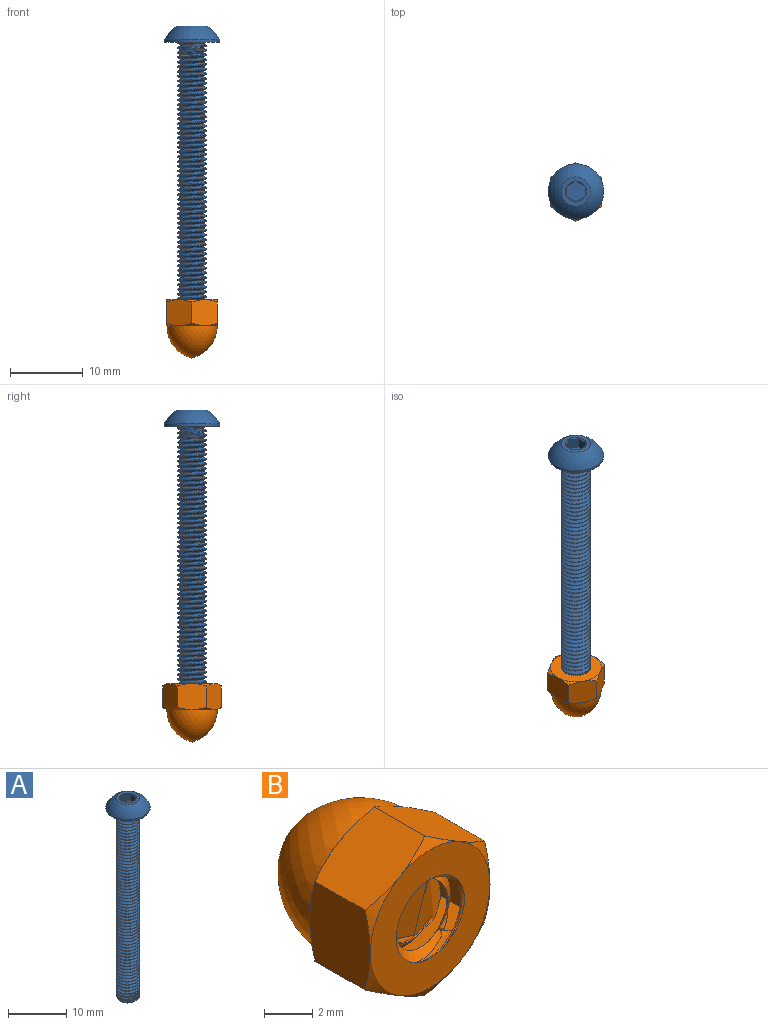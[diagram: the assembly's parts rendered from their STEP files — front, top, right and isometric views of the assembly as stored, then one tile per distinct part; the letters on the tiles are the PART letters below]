
ASSEMBLY  parts=2 mates=1
PART A: 24 faces, bbox 8.2x8.2x43.4 mm
  f0: cone r=1.44mm half-angle=45deg, axis (0,0,1), area 0.2mm2, adj f10,f18
  f1: cylinder r=3.8mm len=7.6mm, axis (0,0,1), area 7.9mm2, adj f2,f11
  f2: sphere r=4.23mm, area 49.8mm2, adj f1,f10
  f3: cone r=1.51mm half-angle=45deg, axis (0,0,1), area 4.2mm2, adj f4,f5,f6,f7,f8
  f4: cylinder r=2mm len=39.51mm, axis (0,0,-1), area 62.1mm2, adj f3,f6,f8,f9,f11
  f5: plane 3.03x3.03mm, normal (0,0,-1), area 7.2mm2, adj f3
  f6: bspline ~40.22x4.63mm, area 339.1mm2, adj f3,f4,f7,f11
  f7: cylinder r=1.58mm len=39.93mm, axis (0,0,-1), area 50.7mm2, adj f3,f6,f8,f11
  f8: bspline ~40.34x4.01mm, area 338.8mm2, adj f3,f4,f7,f9,f11
  f9: plane 0.14x0.08mm, normal (-0.24,0.97,0), area 0mm2, adj f4,f8,f11
  f10: plane 4.47x4.47mm, normal (0,0,1), area 6mm2, adj f0,f2,f12,f13,f14,f15,f16
  f11: plane 7.72x7.72mm, normal (0,0,-1), area 35.1mm2, adj f1,f4,f6,f7,f8,f9
  f12: cone r=1.44mm half-angle=45deg, axis (0,0,1), area 0mm2, adj f10,f19
  f13: cone r=1.44mm half-angle=45deg, axis (0,0,1), area 0mm2, adj f10,f20
  f14: cone r=1.44mm half-angle=45deg, axis (0,0,1), area 0mm2, adj f10,f21
  f15: cone r=1.44mm half-angle=45deg, axis (0,0,1), area 0mm2, adj f10,f22
  f16: cone r=1.44mm half-angle=45deg, axis (0,0,1), area 0mm2, adj f10,f23
  f17: plane 2.89x2.5mm, normal (0,0,1), area 5.4mm2, adj f18,f19,f20,f21,f22,f23
  f18: plane 1.68x1.58mm, normal (-1,0,0), area 2mm2, adj f0,f17,f19,f23
  f19: plane 2.09x1.8mm, normal (-0.5,-0.87,0), area 2mm2, adj f12,f17,f18,f20
  f20: plane 2.09x1.8mm, normal (0.5,-0.87,0), area 2mm2, adj f13,f17,f19,f21
  f21: plane 2.09x1.99mm, normal (1,0,0), area 2mm2, adj f14,f17,f20,f22
  f22: plane 2.09x1.8mm, normal (0.5,0.87,0), area 2mm2, adj f15,f17,f21,f23
  f23: plane 2.09x1.8mm, normal (-0.5,0.87,0), area 2mm2, adj f16,f17,f18,f22
PART B: 34 faces, bbox 8.4x8.6x8.4 mm
  f0: plane 7x7mm, normal (0,1,0), area 0.8mm2, adj f14,f15,f16,f17,f18,f19,f20
  f1: plane 3.89x3.83mm, normal (0.5,0,0.87), area 13.5mm2, adj f2,f6,f10,f11,f17,f18
  f2: plane 4.38x3.89mm, normal (1,0,0), area 13.5mm2, adj f1,f3,f9,f10,f16,f17
  f3: plane 3.89x3.83mm, normal (0.5,0,-0.87), area 13.5mm2, adj f2,f4,f8,f9,f15,f16
  f4: plane 3.89x3.83mm, normal (-0.5,0,-0.87), area 13.5mm2, adj f3,f5,f7,f8,f14,f15
  f5: plane 4.38x3.89mm, normal (-1,0,0), area 13.5mm2, adj f4,f6,f7,f12,f14,f19
  f6: plane 3.89x3.83mm, normal (-0.5,0,0.87), area 13.5mm2, adj f1,f5,f11,f12,f18,f19
  f7: cone r=3.5mm half-angle=60deg, axis (0,1,0), area 1.2mm2, adj f4,f5,f13
  f8: cone r=3.5mm half-angle=60deg, axis (0,1,0), area 1.2mm2, adj f3,f4,f13
  f9: cone r=3.5mm half-angle=60deg, axis (0,1,0), area 1.2mm2, adj f2,f3,f13
  f10: cone r=3.5mm half-angle=60deg, axis (0,1,0), area 1.2mm2, adj f1,f2,f13
  f11: cone r=3.5mm half-angle=60deg, axis (0,1,0), area 1.2mm2, adj f1,f6,f13
  f12: cone r=3.5mm half-angle=60deg, axis (0,1,0), area 1.2mm2, adj f5,f6,f13
  f13: plane 7x7mm, normal (0,-1,0), area 25.9mm2, adj f7,f8,f9,f10,f11,f12,f21,f31
  f14: cone r=3.5mm half-angle=60deg, axis (0,-1,0), area 1.2mm2, adj f0,f4,f5
  f15: cone r=3.5mm half-angle=60deg, axis (0,-1,0), area 1.2mm2, adj f0,f3,f4
  f16: cone r=3.5mm half-angle=60deg, axis (0,-1,0), area 1.2mm2, adj f0,f2,f3
  f17: cone r=3.5mm half-angle=60deg, axis (0,-1,0), area 1.2mm2, adj f0,f1,f2
  f18: cone r=3.5mm half-angle=60deg, axis (0,-1,0), area 1.2mm2, adj f0,f1,f6
  f19: cone r=3.5mm half-angle=60deg, axis (0,-1,0), area 1.2mm2, adj f0,f5,f6
  f20: revolved ~6.93x6.93mm, area 85.3mm2, adj f0
  f21: cylinder r=2mm len=1.55mm, axis (0,-1,0), area 0.1mm2, adj f13,f22,f29
  f22: cylinder r=2mm len=4mm, axis (0,-1,0), area 1.1mm2, adj f21,f23,f28,f29
  f23: cylinder r=2mm len=4mm, axis (0,-1,0), area 1.1mm2, adj f22,f24,f28,f29
  f24: cylinder r=2mm len=4mm, axis (0,-1,0), area 1.1mm2, adj f23,f25,f28,f29
  f25: cylinder r=2mm len=4mm, axis (0,-1,0), area 1.1mm2, adj f24,f26,f28,f29
  f26: cylinder r=2mm len=4mm, axis (0,-1,0), area 1.1mm2, adj f25,f27,f28,f29
  f27: cylinder r=2mm len=4mm, axis (0,-1,0), area 3.5mm2, adj f26,f28,f29,f32,f33
  f28: bspline ~4.62x4.58mm, area 30.8mm2, adj f22,f23,f24,f25,f26,f27,f30,f31
  f29: bspline ~4.62x4.23mm, area 22.7mm2, adj f21,f22,f23,f24,f25,f26,f27,f30
  f30: cylinder r=1.55mm len=3.45mm, axis (0,-1,0), area 4.1mm2, adj f28,f29,f31,f32
  f31: cone r=2mm half-angle=45deg, axis (0,-1,0), area 3.7mm2, adj f13,f28,f29,f30
  f32: plane 4.28x4.28mm, normal (0,1,0), area 2.6mm2, adj f27,f28,f29,f30
  f33: cone r=0mm half-angle=60deg, axis (0,-1,0), area 14.5mm2, adj f27
PLACE A t=(-18.03,-25.55,-14.88)mm
PLACE B rot(axis=(-1,0,0),90deg) t=(-18.03,-25.55,-52.43)mm
MATE fastened B.f7 <-> A.f0  axis (0,0,1) through (-18.03,-25.55,-52.43)mm
